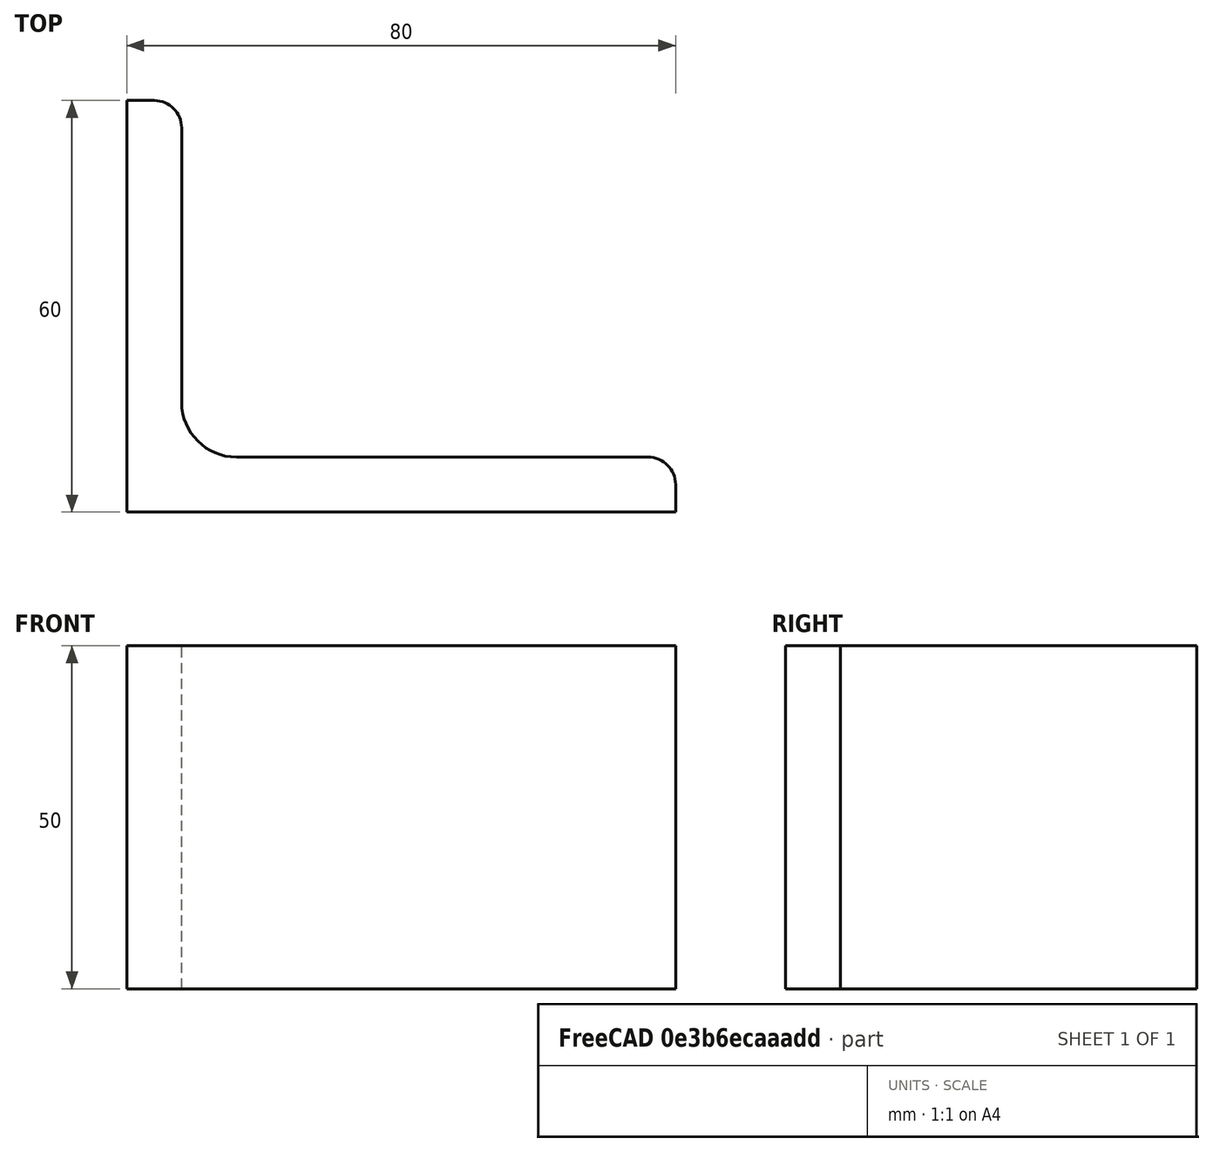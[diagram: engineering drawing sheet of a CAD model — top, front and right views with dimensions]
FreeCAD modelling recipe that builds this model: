
FCSTD DOCUMENT  (FreeCAD 0.15R4671 (Git))
Label: Angle Bar 80x60x8 EN10056 S235JR
License: All rights reserved
LicenseURL: http://en.wikipedia.org/wiki/All_rights_reserved
objects: Sketcher::SketchObject×1, Part::Extrusion×1
note: 2 computed .brp shape members not serialized (recipe doc carries the construction recipe); baked Part::Feature solids carry a one-line shape summary decoded from their .brp

FEATURE [Sketcher::SketchObject] Sketch
  sketch-geometry (9):
    g0: LineSegment StartX=0 StartY=0 StartZ=0 EndX=80 EndY=0 EndZ=0
    g1: LineSegment StartX=80 StartY=0 StartZ=0 EndX=80 EndY=4 EndZ=0
    g2: LineSegment StartX=76 StartY=8 StartZ=0 EndX=16 EndY=8 EndZ=0
    g3: LineSegment StartX=0 StartY=0 StartZ=0 EndX=0 EndY=60 EndZ=0
    g4: LineSegment StartX=0 StartY=60 StartZ=0 EndX=4 EndY=60 EndZ=0
    g5: LineSegment StartX=8 StartY=56 StartZ=0 EndX=8 EndY=16 EndZ=0
    g6: ArcOfCircle CenterX=16 CenterY=16 CenterZ=0 NormalX=0 NormalY=0 NormalZ=1 Radius=8 StartAngle=3.14159 EndAngle=4.71239
    g7: ArcOfCircle CenterX=4 CenterY=56 CenterZ=0 NormalX=0 NormalY=0 NormalZ=1 Radius=4 StartAngle=0 EndAngle=1.5708
    g8: ArcOfCircle CenterX=76 CenterY=4 CenterZ=0 NormalX=0 NormalY=0 NormalZ=1 Radius=4 StartAngle=0 EndAngle=1.5708
  constraints (23):
    c: Coincident(g0,g-1)
    c: Horizontal(g0)
    c: Coincident(g1,g0)
    c: Vertical(g1)
    c: Horizontal(g2)
    c: Coincident(g3,g-1)
    c: Vertical(g3)
    c: Coincident(g4,g3)
    c: Horizontal(g4)
    c: Vertical(g5)
    c: Tangent(g5,g6) = -1.5708
    c: Tangent(g2,g6) = 1.5708
    c: Tangent(g4,g7) = 1.5708
    c: Tangent(g5,g7) = 1.5708
    c: Tangent(g2,g8) = -1.5708
    c: Tangent(g1,g8) = -1.5708
    c: DistanceX(g0) = 80
    c: DistanceY(g3) = 60
    c: DistanceY(g0,g2) = 8
    c: DistanceX(g3,g5) = 8
    c: Radius(g6) = 8
    c: Radius(g8) = 4
    c: Radius(g7) = 4
FEATURE [Part::Extrusion] Extrude  label="Angle Bar 80x60x8 EN10056 S235JR"
  Base = -> Sketch
  Dir = (0,0,50)
  Solid = true
